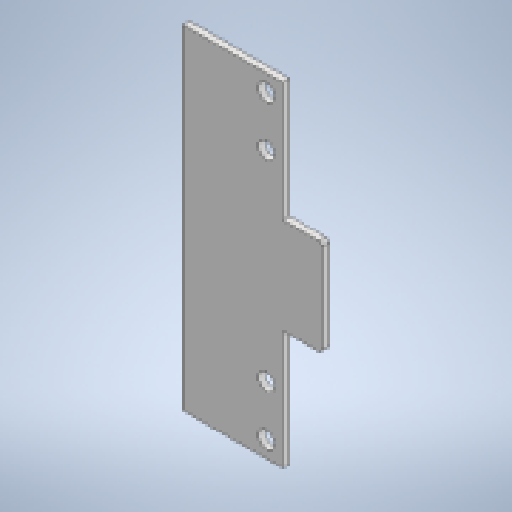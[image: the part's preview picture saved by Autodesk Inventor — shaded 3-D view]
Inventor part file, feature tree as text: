
AUTODESK INVENTOR PART (.ipt)
format: ipt  version: 2025 (Build 290162010, 162A)  size: 283,648 bytes
history: native  units: mm
features: sketch x2, sheet_metal_op x1, hole x1, fillet x1, other x1, projected_geometry x1
ambient origin geometry x8: Origin, YZ Plane, XZ Plane, XY Plane, X Axis, Y Axis, Z Axis, Center Point
bodies: Solid1 (feature_tree)
feature tree (7):
  sheet_metal_op  "Face1"
  hole  "Hole1"  [1 undecoded]
  fillet  "Fillet1"  Radius=120.0mm
  sketch  "Sketch1"  dims[d2=8.0mm]
  other  "Plate1"
  sketch  "Sketch2"  dims[d3=20.0mm d4=6.0mm d5=4.0mm d6=2.0mm d7=90.0deg d8=8.0mm d9=20.594885mm d16=120.0mm d17=400.0mm d19=20.0mm d20=20.0mm d21=360.0mm d22=120.0mm d23=120.0mm d24=47.0mm d25=115.0mm d26=4.0mm]
  projected_geometry  "Projected Loop1"
note: 1 required parameter value undecoded (feature->parameter linkage not recoverable at this tier; creation-order binding heuristic only, values carry confidence <= 0.55)
